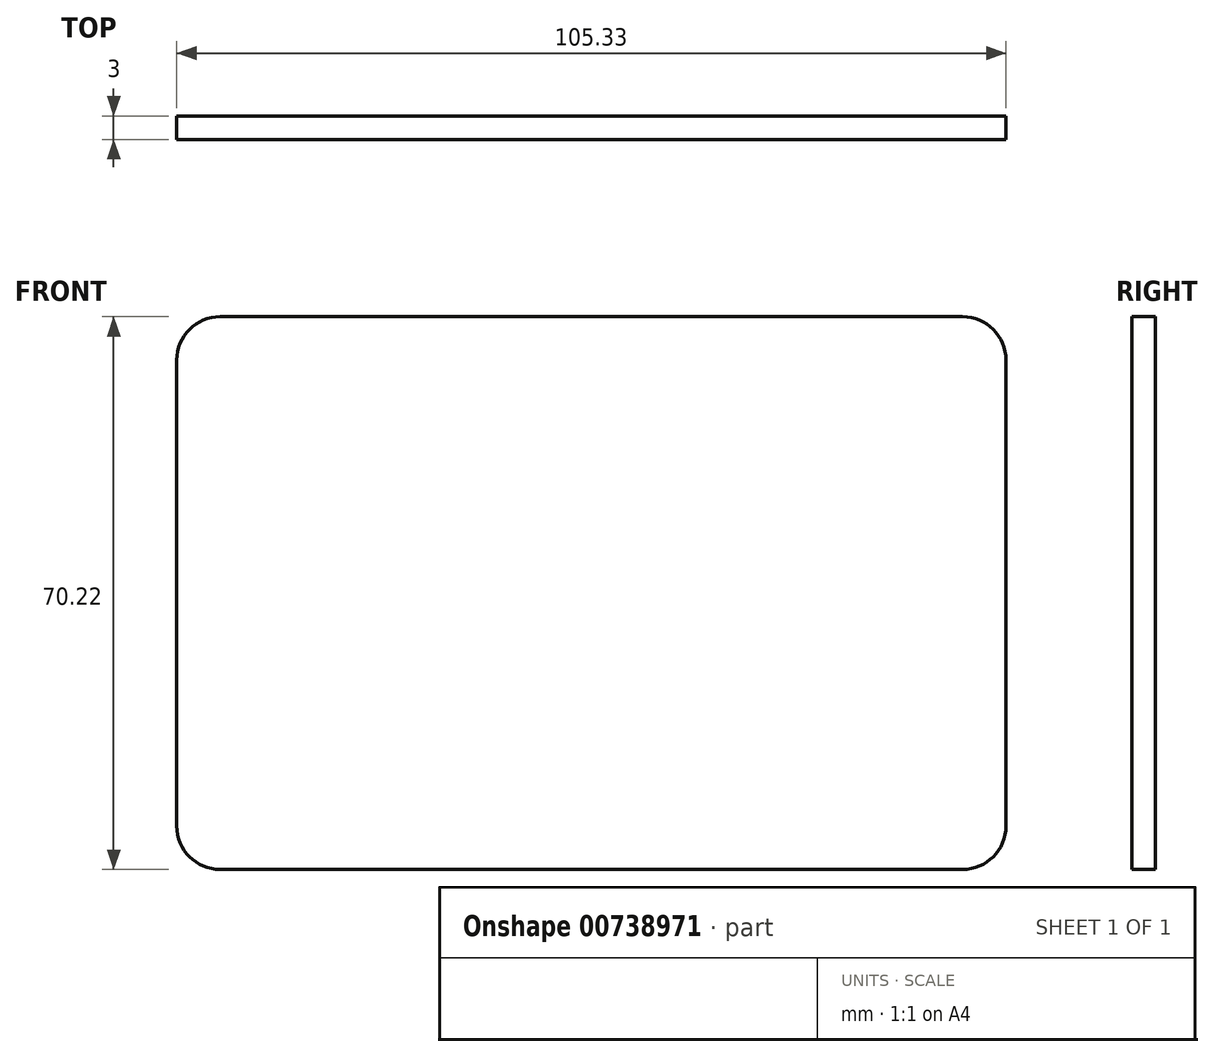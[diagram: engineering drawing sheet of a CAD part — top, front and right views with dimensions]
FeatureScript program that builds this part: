
annotation { "Feature Type Name" : "Feature", "Feature Type Description" : "" }
export const myFeature = defineFeature(function(context is Context, id is Id, definition is map)
    precondition{}
    {
        {
            var Q0;
            Q0=qCreatedBy(makeId("Front.planeOp"),FACE);
            var sketch = newSketch(context, id + "F0", { "sketchPlane" : qUnion([Q0])});
            skLineSegment(sketch, "E0", {"start": v(-345.32, 35.87) * mm, "end": v(-251.01, 35.87) * mm});
            skLineSegment(sketch, "E1", {"start": v(-245.5, 30.36) * mm, "end": v(-245.5, -28.84) * mm});
            skLineSegment(sketch, "E2", {"start": v(-251.01, -34.35) * mm, "end": v(-345.32, -34.35) * mm});
            skLineSegment(sketch, "E3", {"start": v(-350.83, -28.84) * mm, "end": v(-350.83, 30.36) * mm});
            skPoint(sketch, "E4.visualSharp", {"position": v(-350.83, 35.87) * mm});
            skArc(sketch, "E4.filletArc", {"start": v(-345.32, 35.87) * mm, "mid": v(-349.21, 34.25) * mm, "end": v(-350.83, 30.36) * mm});
            skPoint(sketch, "E5.visualSharp", {"position": v(-245.5, 35.87) * mm});
            skArc(sketch, "E5.filletArc", {"start": v(-245.5, 30.36) * mm, "mid": v(-247.12, 34.25) * mm, "end": v(-251.01, 35.87) * mm});
            skPoint(sketch, "E6.visualSharp", {"position": v(-245.5, -34.35) * mm});
            skArc(sketch, "E6.filletArc", {"start": v(-251.01, -34.35) * mm, "mid": v(-247.12, -32.73) * mm, "end": v(-245.5, -28.84) * mm});
            skPoint(sketch, "E7.visualSharp", {"position": v(-350.83, -34.35) * mm});
            skArc(sketch, "E7.filletArc", {"start": v(-350.83, -28.84) * mm, "mid": v(-349.21, -32.73) * mm, "end": v(-345.32, -34.35) * mm});
            skSolve(sketch);
        }
        {
            var Q0;
            Q0=makeQuery(id+"F0.imprint","IMPRINT",FACE,{"disambiguationData":[TD([[makeQuery(id+"F0.imprint","IMPRINT",EDGE,{"derivedFrom":sQuery(id+"F0.wireOp",EDGE,"E0")}),-1.0]])]});
            extrude(context, id + "F1", {"entities" : qUnion([Q0]), "depth" : 3 * mm, "offsetDistance" : 25 * mm});
        }
    });
